# Revit family: TV-200-C
name_source: partatom
category: Aparatos sanitarios
units: mm (PartAtom-declared; Revit-internal decimal feet)

## family parameters
Compartido = No
Corte con vacíos al cargar = No
Cota de conector redondo = Diámetro de uso
Número OmniClass = 23.45.00.00
Punto de cálculo de habitación = No
Se basa en plano de trabajo = No
Siempre vertical = Sí
Tipo de pieza = Normal
Título OmniClass = Sanitary, Laundry, and Cleaning Equipment

## types (1)
- TV-200-C
    Batteries = DL-223 Duracell Lithium Battery Or CRP2 (Panasonic)
    Chrome = Brass Chromed
    Comentarios de tipo = Línea Elecrónica
    Conexión AC = Sí
    Conexión AF = Sí
    Descripción = Llave de lavabo electrónica de sensor de corriente
a pared.
    Detection Range = 1.9" (50 mm) - 9.4" (240 mm)
    Elevación por defecto = 0"
    Fabricante = Helvex
    Feeding Voltage = 6 V
    Inlet Threads = ½" - 14 NPSM
    Max. Water Flow = 0.5 gal/min
    Max. Working Pressure = 85.3 psi
    Min. Working Pressure = 5.7 psi
    Modelo = TV-200-C

## geometry (parser evidence)
native form markers: Sweep x3
no freeform markers — native parametric forms only
